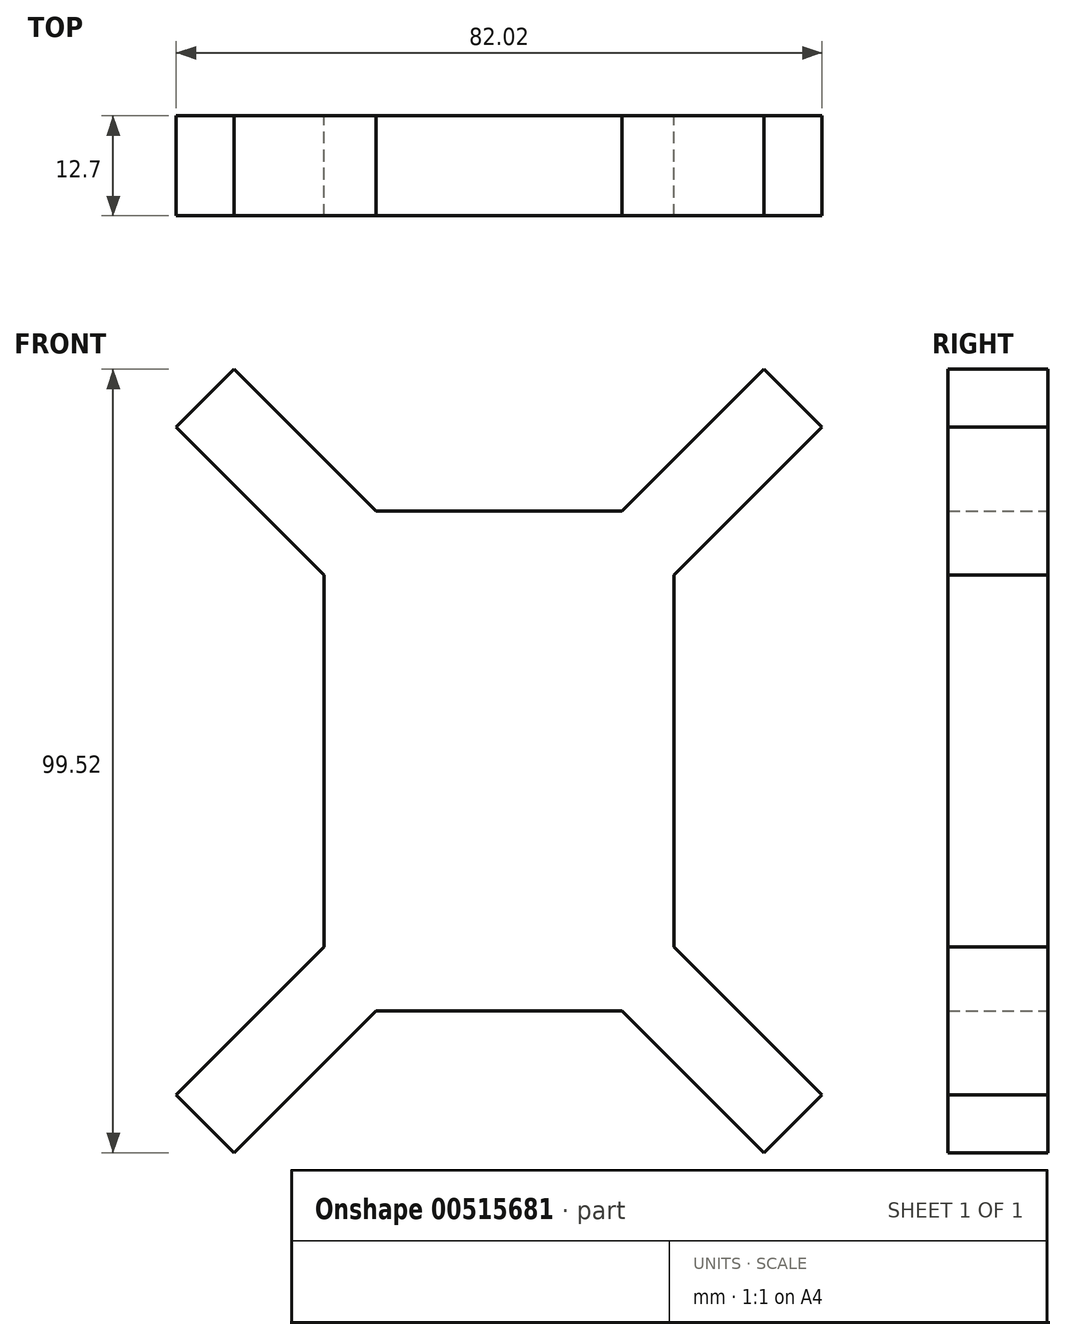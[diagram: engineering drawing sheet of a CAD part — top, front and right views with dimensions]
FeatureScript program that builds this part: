
annotation { "Feature Type Name" : "Feature", "Feature Type Description" : "" }
export const myFeature = defineFeature(function(context is Context, id is Id, definition is map)
    precondition{}
    {
        {
            var Q0;
            Q0=qCreatedBy(makeId("Front.planeOp"),FACE);
            var sketch = newSketch(context, id + "F0", { "sketchPlane" : qUnion([Q0])});
            skLineSegment(sketch, "E0.bottom", {"start": v(22.23, 31.75) * mm, "end": v(-22.23, 31.75) * mm});
            skLineSegment(sketch, "E0.top", {"start": v(22.22, -31.75) * mm, "end": v(-22.23, -31.75) * mm});
            skLineSegment(sketch, "E0.left", {"start": v(22.23, 31.75) * mm, "end": v(22.22, -31.75) * mm});
            skLineSegment(sketch, "E0.right", {"start": v(-22.22, 31.75) * mm, "end": v(-22.23, -31.75) * mm});
            skPoint(sketch, "E0.middle", {"position": v(0, 0) * mm});
            skLineSegment(sketch, "E1", {"start": v(19.45, -20.84) * mm, "end": v(41, -42.4) * mm});
            skLineSegment(sketch, "E2", {"start": v(41, -42.4) * mm, "end": v(33.64, -49.76) * mm});
            skLineSegment(sketch, "E3", {"start": v(33.64, -49.76) * mm, "end": v(12.09, -28.2) * mm});
            skLineSegment(sketch, "E4", {"start": v(12.09, -28.2) * mm, "end": v(19.45, -20.84) * mm});
            skLineSegment(sketch, "E5.MirrorCS", {"start": v(-19.45, -20.84) * mm, "end": v(-41, -42.4) * mm});
            skLineSegment(sketch, "E6.MirrorCS", {"start": v(-33.64, -49.76) * mm, "end": v(-12.09, -28.2) * mm});
            skLineSegment(sketch, "E7.MirrorCS", {"start": v(-12.09, -28.2) * mm, "end": v(-19.45, -20.84) * mm});
            skLineSegment(sketch, "E8.MirrorCS", {"start": v(-41, -42.4) * mm, "end": v(-33.64, -49.76) * mm});
            skLineSegment(sketch, "E9.MirrorCS", {"start": v(19.45, 20.84) * mm, "end": v(41, 42.4) * mm});
            skLineSegment(sketch, "E10.MirrorCS", {"start": v(33.64, 49.76) * mm, "end": v(12.09, 28.2) * mm});
            skLineSegment(sketch, "E11.MirrorCS", {"start": v(41, 42.4) * mm, "end": v(33.64, 49.76) * mm});
            skLineSegment(sketch, "E12.MirrorCS", {"start": v(12.09, 28.2) * mm, "end": v(19.45, 20.84) * mm});
            skLineSegment(sketch, "E13.MirrorCS", {"start": v(-19.45, 20.84) * mm, "end": v(-41, 42.4) * mm});
            skLineSegment(sketch, "E14.MirrorCS", {"start": v(-12.09, 28.2) * mm, "end": v(-19.45, 20.84) * mm});
            skLineSegment(sketch, "E15.MirrorCS", {"start": v(-33.64, 49.76) * mm, "end": v(-12.09, 28.2) * mm});
            skLineSegment(sketch, "E16.MirrorCS", {"start": v(-41, 42.4) * mm, "end": v(-33.64, 49.76) * mm});
            skSolve(sketch);
        }
        {
            var Q0;
            {var subQ1=sQuery(id+"F0.wireOp",EDGE,"E4");Q0=makeQuery(id+"F0.imprint","IMPRINT",FACE,{"disambiguationData":[TD([[makeQuery(id+"F0.imprint","IMPRINT",EDGE,{"derivedFrom":subQ1}),1.0]])]});}
            var Q1;
            {var subQ0=sQuery(id+"F0.wireOp",EDGE,"E16.MirrorCS");Q1=makeQuery(id+"F0.imprint","IMPRINT",FACE,{"disambiguationData":[TD([[makeQuery(id+"F0.imprint","IMPRINT",EDGE,{"derivedFrom":subQ0}),-1.0]])]});}
            var Q2;
            {var subQ0=sQuery(id+"F0.wireOp",EDGE,"E2");Q2=makeQuery(id+"F0.imprint","IMPRINT",FACE,{"disambiguationData":[TD([[makeQuery(id+"F0.imprint","IMPRINT",EDGE,{"derivedFrom":subQ0}),-1.0]])]});}
            var Q3;
            {var subQ0=sQuery(id+"F0.wireOp",EDGE,"E8.MirrorCS");Q3=makeQuery(id+"F0.imprint","IMPRINT",FACE,{"disambiguationData":[TD([[makeQuery(id+"F0.imprint","IMPRINT",EDGE,{"derivedFrom":subQ0}),1.0]])]});}
            var Q4;
            {var subQ0=sQuery(id+"F0.wireOp",EDGE,"E11.MirrorCS");Q4=makeQuery(id+"F0.imprint","IMPRINT",FACE,{"disambiguationData":[TD([[makeQuery(id+"F0.imprint","IMPRINT",EDGE,{"derivedFrom":subQ0}),1.0]])]});}
            var Q5;
            {var subQ0=sQuery(id+"F0.wireOp",EDGE,"E4");Q5=makeQuery(id+"F0.imprint","IMPRINT",FACE,{"disambiguationData":[TD([[makeQuery(id+"F0.imprint","IMPRINT",EDGE,{"derivedFrom":subQ0}),-1.0]])]});}
            var Q6;
            {var subQ0=sQuery(id+"F0.wireOp",EDGE,"E7.MirrorCS");Q6=makeQuery(id+"F0.imprint","IMPRINT",FACE,{"disambiguationData":[TD([[makeQuery(id+"F0.imprint","IMPRINT",EDGE,{"derivedFrom":subQ0}),1.0]])]});}
            var Q7;
            {var subQ0=sQuery(id+"F0.wireOp",EDGE,"E14.MirrorCS");Q7=makeQuery(id+"F0.imprint","IMPRINT",FACE,{"disambiguationData":[TD([[makeQuery(id+"F0.imprint","IMPRINT",EDGE,{"derivedFrom":subQ0}),-1.0]])]});}
            var Q8;
            {var subQ0=sQuery(id+"F0.wireOp",EDGE,"E12.MirrorCS");Q8=makeQuery(id+"F0.imprint","IMPRINT",FACE,{"disambiguationData":[TD([[makeQuery(id+"F0.imprint","IMPRINT",EDGE,{"derivedFrom":subQ0}),1.0]])]});}
            extrude(context, id + "F1", {"entities" : qUnion([Q0, Q1, Q2, Q3, Q4, Q5, Q6, Q7, Q8]), "endBound" : BoundingType.SYMMETRIC, "depth" : 12.7 * mm, "offsetDistance" : 25.4 * mm});
        }
    });
